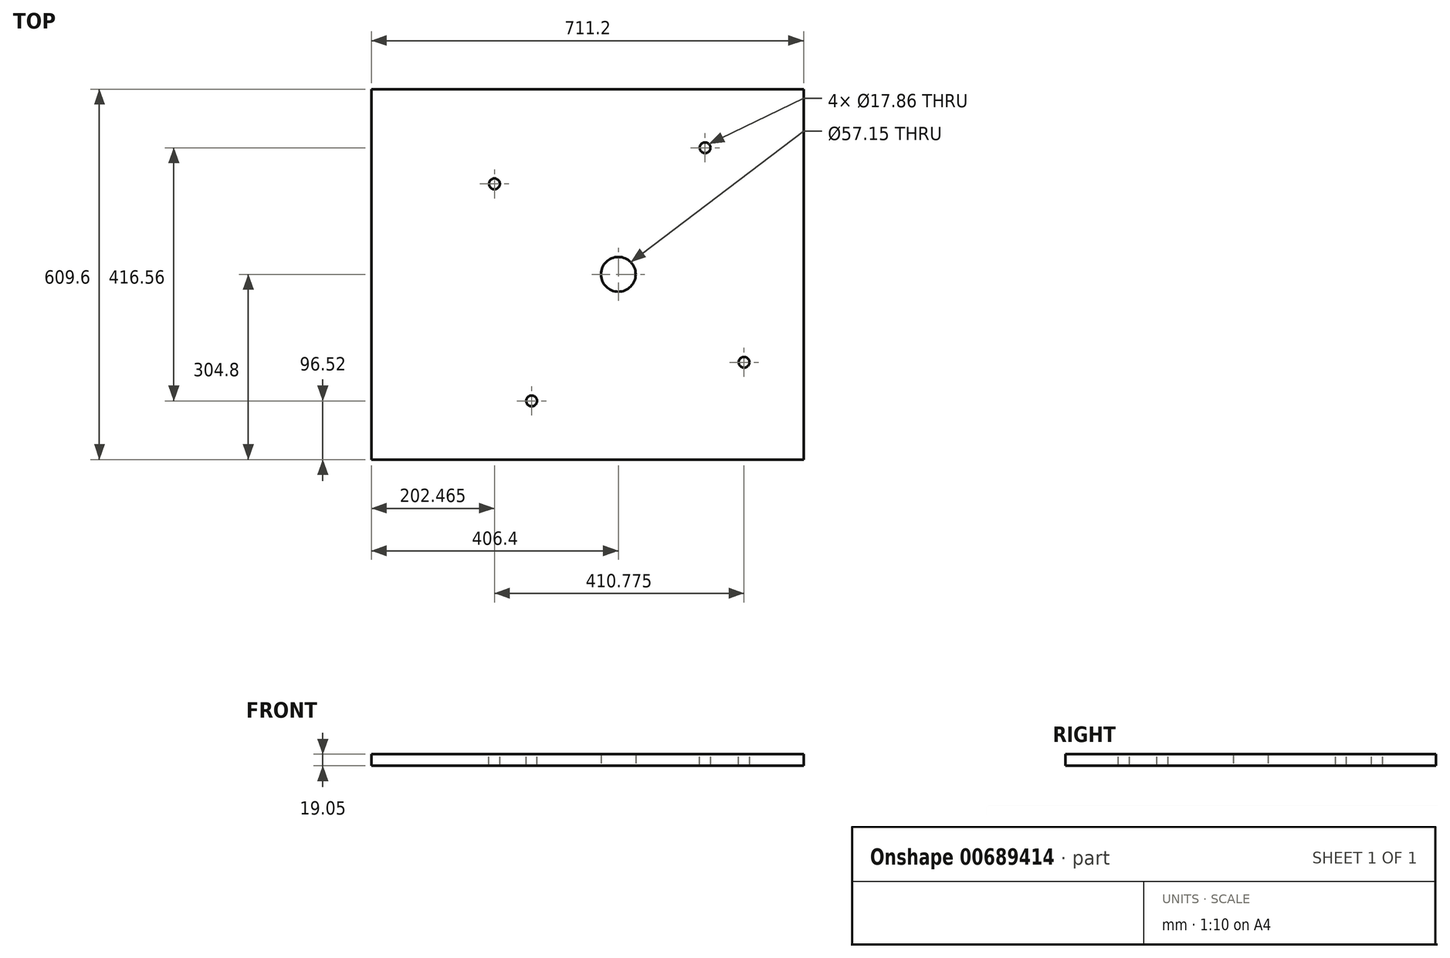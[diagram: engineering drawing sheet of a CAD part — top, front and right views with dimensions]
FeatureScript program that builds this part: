
annotation { "Feature Type Name" : "Feature", "Feature Type Description" : "" }
export const myFeature = defineFeature(function(context is Context, id is Id, definition is map)
    precondition{}
    {
        {
            var Q0;
            Q0=qCreatedBy(makeId("Top.planeOp"),FACE);
            var sketch = newSketch(context, id + "F0", { "sketchPlane" : qUnion([Q0])});
            skLineSegment(sketch, "E0.bottom", {"start": v(-355.6, 304.8) * mm, "end": v(355.6, 304.8) * mm});
            skLineSegment(sketch, "E0.top", {"start": v(-355.6, -304.8) * mm, "end": v(355.6, -304.8) * mm});
            skLineSegment(sketch, "E0.left", {"start": v(-355.6, 304.8) * mm, "end": v(-355.6, -304.8) * mm});
            skLineSegment(sketch, "E0.right", {"start": v(355.6, 304.8) * mm, "end": v(355.6, -304.8) * mm});
            skPoint(sketch, "E0.middle", {"position": v(0, 0) * mm});
            skCircle(sketch, "E1", {"center": v(50.8, 0) * mm, "radius": 28.58 * mm});
            skSolve(sketch);
        }
        {
            var Q0;
            Q0=makeQuery(id+"F0.imprint","IMPRINT",FACE,{"disambiguationData":[TD([[makeQuery(id+"F0.imprint","IMPRINT",EDGE,{"derivedFrom":sQuery(id+"F0.wireOp",EDGE,"E0.bottom")}),-1.0]])]});
            extrude(context, id + "F1", {"entities" : qUnion([Q0]), "depth" : 19.05 * mm, "offsetDistance" : 25.4 * mm});
        }
        {
            var Q0;
            Q0=makeQuery(id+"F1.opExtrude","CAP_FACE",FACE,{"disambiguationData":[OSD([sQuery(id+"F0.wireOp",EDGE,"E0.bottom"),sQuery(id+"F0.wireOp",EDGE,"E0.top"),sQuery(id+"F0.wireOp",EDGE,"E0.left"),sQuery(id+"F0.wireOp",EDGE,"E0.right"),sQuery(id+"F0.wireOp",EDGE,"E1")])],"isStart":false});
            var sketch = newSketch(context, id + "F2", { "sketchPlane" : qUnion([Q0])});
            skPoint(sketch, "E2", {"position": v(257.64, -144.78) * mm});
            skPoint(sketch, "E3", {"position": v(-91.9, -208.28) * mm});
            skPoint(sketch, "E4", {"position": v(-153.14, 148.84) * mm});
            skPoint(sketch, "E5", {"position": v(193.5, 208.28) * mm});
            skSolve(sketch);
        }
        {
            var Q0;
            Q0=sQuery(id+"F2.wireOp",VERTEX,"E4");
            var Q1;
            Q1=sQuery(id+"F2.wireOp",VERTEX,"E3");
            var Q2;
            Q2=sQuery(id+"F2.wireOp",VERTEX,"E2");
            var Q3;
            Q3=sQuery(id+"F2.wireOp",VERTEX,"E5");
            var Q4;
            Q4=makeQuery(id+"F1.opExtrude","SWEPT_BODY",BODY,{"disambiguationData":[OSD([sQuery(id+"F0.wireOp",EDGE,"E0.bottom"),sQuery(id+"F0.wireOp",EDGE,"E0.top"),sQuery(id+"F0.wireOp",EDGE,"E0.left"),sQuery(id+"F0.wireOp",EDGE,"E0.right"),sQuery(id+"F0.wireOp",EDGE,"E1")])]});
            hole(context, id + "F3", {"style" : HoleStyle.SIMPLE, "endStyle" : HoleEndStyle.THROUGH, "standardTappedOrClearance" : lookupTablePath({ "standard" : "ANSI", "engagement" : "75%", "pitch" : "20 tpi", "size" : "3/4", "type" : "Tapped" }), "standardBlindInLast" : lookupTablePath({ "standard" : "ANSI", "engagement" : "75%", "pitch" : "20 tpi", "size" : "3/4", "type" : "Tapped" }), "holeDiameter" : 17.86 * mm, "majorDiameter" : 19.05 * mm, "showTappedDepth" : true, "tappedDepth" : 10.3 * mm, "tapClearance" : 3, "locations" : qUnion([Q0, Q1, Q2, Q3]), "scope" : qUnion([Q4])});
        }
    });
